# Revit family: 3033702 Feilo Sylvania Lighting Fixture INSAVER150 HO TOPPER LED SQ 12W WW
name_source: partatom
category: Lighting Fixtures
revit_build: Autodesk Revit 2017 (Build: 20190507_1515(x64)
units: mm (PartAtom-declared; Revit-internal decimal feet)

## family parameters
Cut with Voids When Loaded = No
Host = Face
Light Source = Yes
OmniClass Number = 23.80.70.00
OmniClass Title = Lighting
Part Type = Normal
Room Calculation Point = No
Round Connector Dimension = Use Diameter
Shared = No

## types (1)
- 3033702 INSAVER150 HO TOPPER LED SQ 12W WW
    Apparent Load = 12 VA
    Assembly Code = D5020200
    AssetType = Fixed
    ClassificationName = Uniclass2015
    ClassificationValue = EF_70_80
    Color Filter = 16777215
    Cost = 0 $
    Default Elevation = 1219 mm
    Dimming Lamp Color Temperature Shift = <None>
    DocumentationLiterature = http://www.sylvania-lighting.com
    DurationUnit = hours
    Emit Shape Visible in Rendering = No
    Emit from Rectangle Length = 132 mm
    Emit from Rectangle Width = 132 mm
    ExpectedLife = 50000
    HeightBlend_FEILO = 48 mm
    HeightMiddle_FEILO = 8 mm  [stored 0.0262467 ft]
    HeightRecessed_FEILO = 68 mm
    HieghtBezel_FEILO = 4 mm  [stored 0.0131234 ft]
    HieghtCutOut_FEILO = 85 mm
    IfcExportAs = IfcLightFixtureType
    IfcExportType = IfcLightFixtureType
    ImpactProtectionIndex = IK02
    IngressProtection = IP44
    InputVoltage = 220-240V~
    Keynote = 16500
    Lamp = LED
    LampColourRenderingIndex = 0
    LampColourTemperature = 3000 K
    LampNominalLuminous = 874 lm
    LampsType = LED
    LuminousEfficacy = 73 lm/W
    Manufacturer = Feilo Sylvania
    ManufacturerName = Feilo Sylvania
    Material = polycarbonate diffuser
    Material_1_FEILO = Bezel-Sylvania-InsaverHoTopperSquare-White
    Material_2_FEILO = Body-Sylvania-InsaverHoTopperSquare-Black
    Material_3_FEILO = Diffuser-Sylvania-InsaverHoTopperSquare
    Material_4_FEILO = <By Category>
    Model = INSAVER150 HO TOPPER LED SQ 12W WW
    ModelNumber = 3033702
    ModelReference = INSAVER150 HO TOPPER LED SQ 12W WW
    Name = INSAVER150 HO TOPPER LED SQ 12W WW
    NominalDepth = 150 mm
    NominalHeight = 68 mm
    NominalLength = 150 mm
    Offset1_FEILO = 3 mm  [stored 0.00984252 ft]
    Offset2_FEILO = 6 mm  [stored 0.019685 ft]
    Offset3_FEILO = 20 mm
    Photometric Web File = 3033702.ies
    PowerConsumption = 12 W
    PowerFactor = 0
    Tilt Angle = -90.00°
    Type Image = <None>
    TypeName = INSAVER150 HO TOPPER LED SQ 12W WW
    URL = http://www.sylvania-lighting.com
    Voltage = 230 V
    Weight = 7.8 kg
    WidthCutOut_FEILO = 150 mm
    Width_FEILO = 170 mm  [stored 0.557743 ft]

note: [stored X ft] marks values corroborated as IEEE doubles in the binary element streams (Revit-internal decimal feet)

## geometry (parser evidence)
native form markers: Blend x1, Sweep x2
no freeform markers — native parametric forms only
